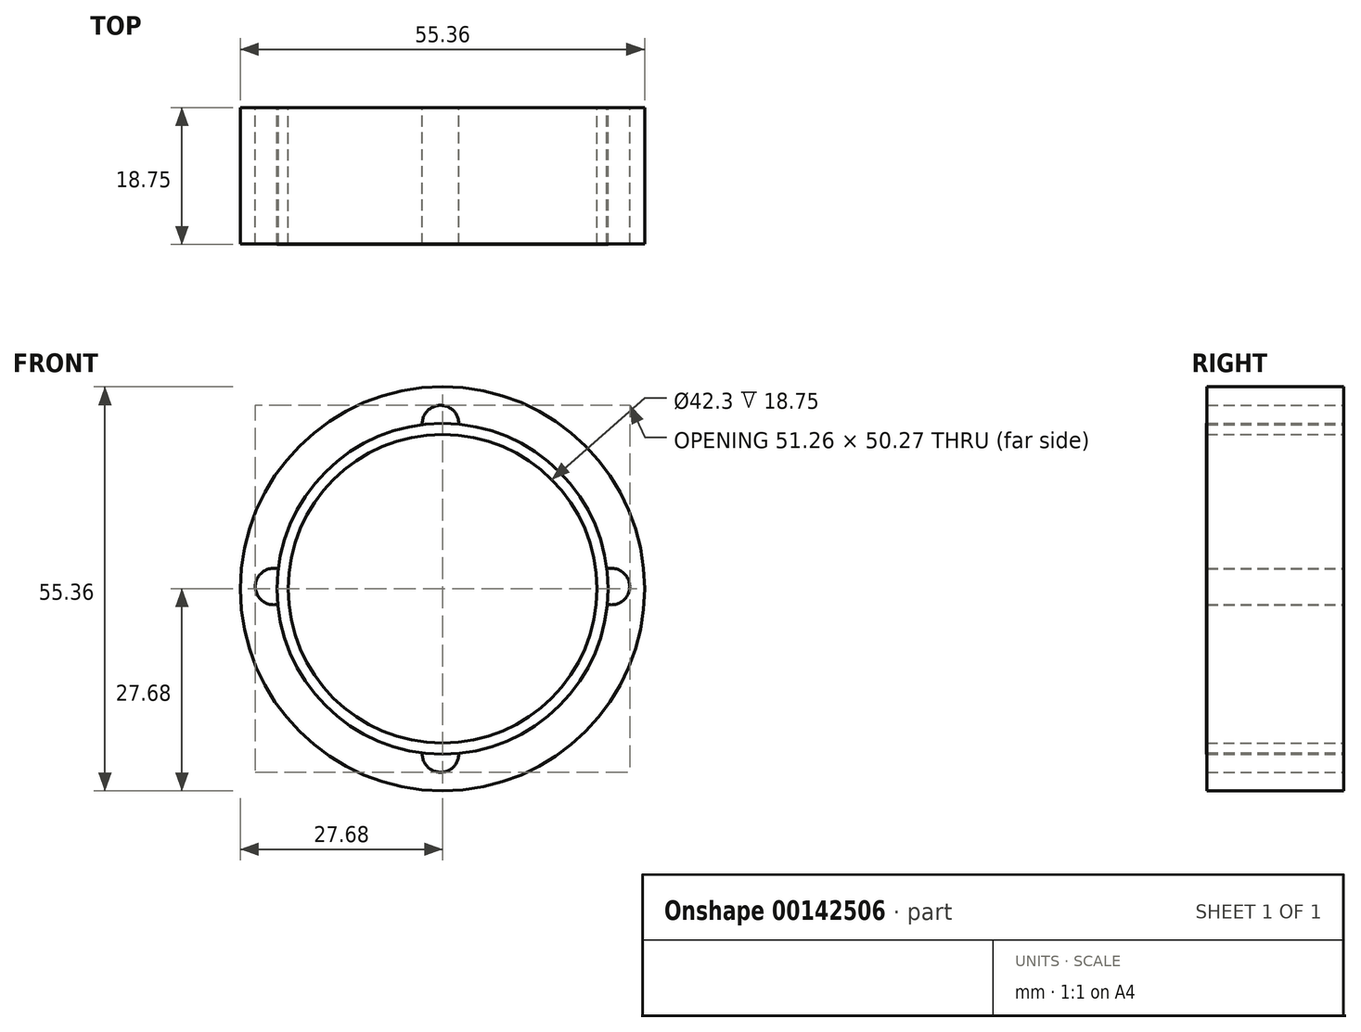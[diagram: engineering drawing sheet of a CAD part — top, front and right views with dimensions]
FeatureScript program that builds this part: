
annotation { "Feature Type Name" : "Feature", "Feature Type Description" : "" }
export const myFeature = defineFeature(function(context is Context, id is Id, definition is map)
    precondition{}
    {
        {
            var Q0;
            Q0=qCreatedBy(makeId("Front.planeOp"),FACE);
            var sketch = newSketch(context, id + "F0", { "sketchPlane" : qUnion([Q0])});
            skCircle(sketch, "E0", {"center": v(0, 0) * mm, "radius": 27.68 * mm});
            skCircle(sketch, "E1", {"center": v(0, 0) * mm, "radius": 21.15 * mm});
            skCircle(sketch, "E2", {"center": v(0, 0) * mm, "radius": 22.65 * mm});
            skArc(sketch, "E3", {"start": v(1.68, 21.08) * mm, "mid": v(-0.3, 25.14) * mm, "end": v(-2.2, 21.04) * mm});
            skArc(sketch, "E4", {"start": v(-21.08, 1.74) * mm, "mid": v(-25.63, 0.34) * mm, "end": v(-21.12, -1.17) * mm});
            skArc(sketch, "E5", {"start": v(-2.2, -21.04) * mm, "mid": v(-0.3, -25.14) * mm, "end": v(1.68, -21.08) * mm});
            skArc(sketch, "E6", {"start": v(21.12, -1.17) * mm, "mid": v(25.63, 0.34) * mm, "end": v(21.08, 1.74) * mm});
            skSolve(sketch);
        }
        {
            var Q0;
            Q0 = qSketchRegion(id + "F0", true);
            extrude(context, id + "F1", {"entities" : qUnion([Q0]), "depth" : 18.7 * mm});
        }
        {
            var Q0;
            Q0=makeQuery(id+"F0.imprint","IMPRINT",FACE,{"disambiguationData":[TD([[makeQuery(id+"F0.imprint","IMPRINT",EDGE,{"derivedFrom":sQuery(id+"F0.wireOp",EDGE,"E1")}),-1.0]])]});
            extrude(context, id + "F2", {"entities" : qUnion([Q0]), "depth" : 18.75 * mm});
        }
    });
